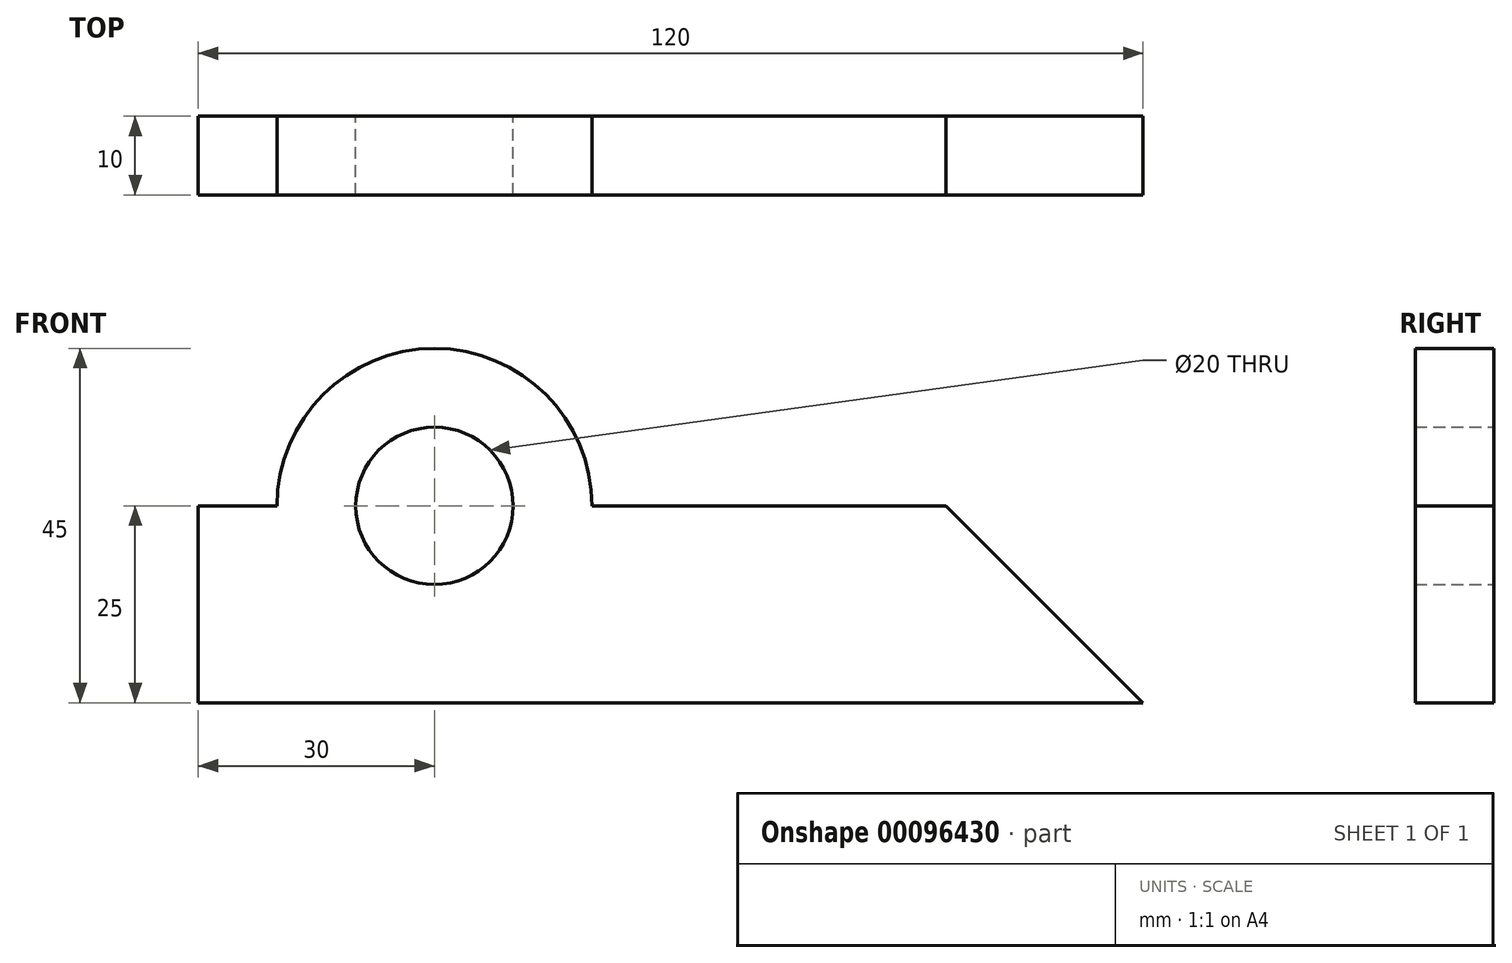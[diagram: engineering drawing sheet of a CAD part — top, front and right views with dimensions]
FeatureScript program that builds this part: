
annotation { "Feature Type Name" : "Feature", "Feature Type Description" : "" }
export const myFeature = defineFeature(function(context is Context, id is Id, definition is map)
    precondition{}
    {
        {
            var Q0;
            Q0=qCreatedBy(makeId("Front.planeOp"),FACE);
            var sketch = newSketch(context, id + "F0", { "sketchPlane" : qUnion([Q0])});
            skLineSegment(sketch, "E0", {"start": v(0, 0) * mm, "end": v(0, 25) * mm});
            skLineSegment(sketch, "E1", {"start": v(0, 0) * mm, "end": v(120, 0) * mm});
            skLineSegment(sketch, "E2", {"start": v(120, 0) * mm, "end": v(95, 25) * mm});
            skLineSegment(sketch, "E3", {"start": v(95, 25) * mm, "end": v(50, 25) * mm});
            skLineSegment(sketch, "E4", {"start": v(0, 25) * mm, "end": v(10, 25) * mm});
            skArc(sketch, "E5", {"start": v(50, 25) * mm, "mid": v(30, 45) * mm, "end": v(10, 25) * mm});
            skCircle(sketch, "E6", {"center": v(30, 25) * mm, "radius": 10 * mm});
            skSolve(sketch);
        }
        {
            var Q0;
            Q0=makeQuery(id+"F0.imprint","IMPRINT",FACE,{"disambiguationData":[TD([[makeQuery(id+"F0.imprint","IMPRINT",EDGE,{"derivedFrom":sQuery(id+"F0.wireOp",EDGE,"E0")}),-1.0]])]});
            extrude(context, id + "F1", {"entities" : qUnion([Q0]), "depth" : 10 * mm});
        }
    });
